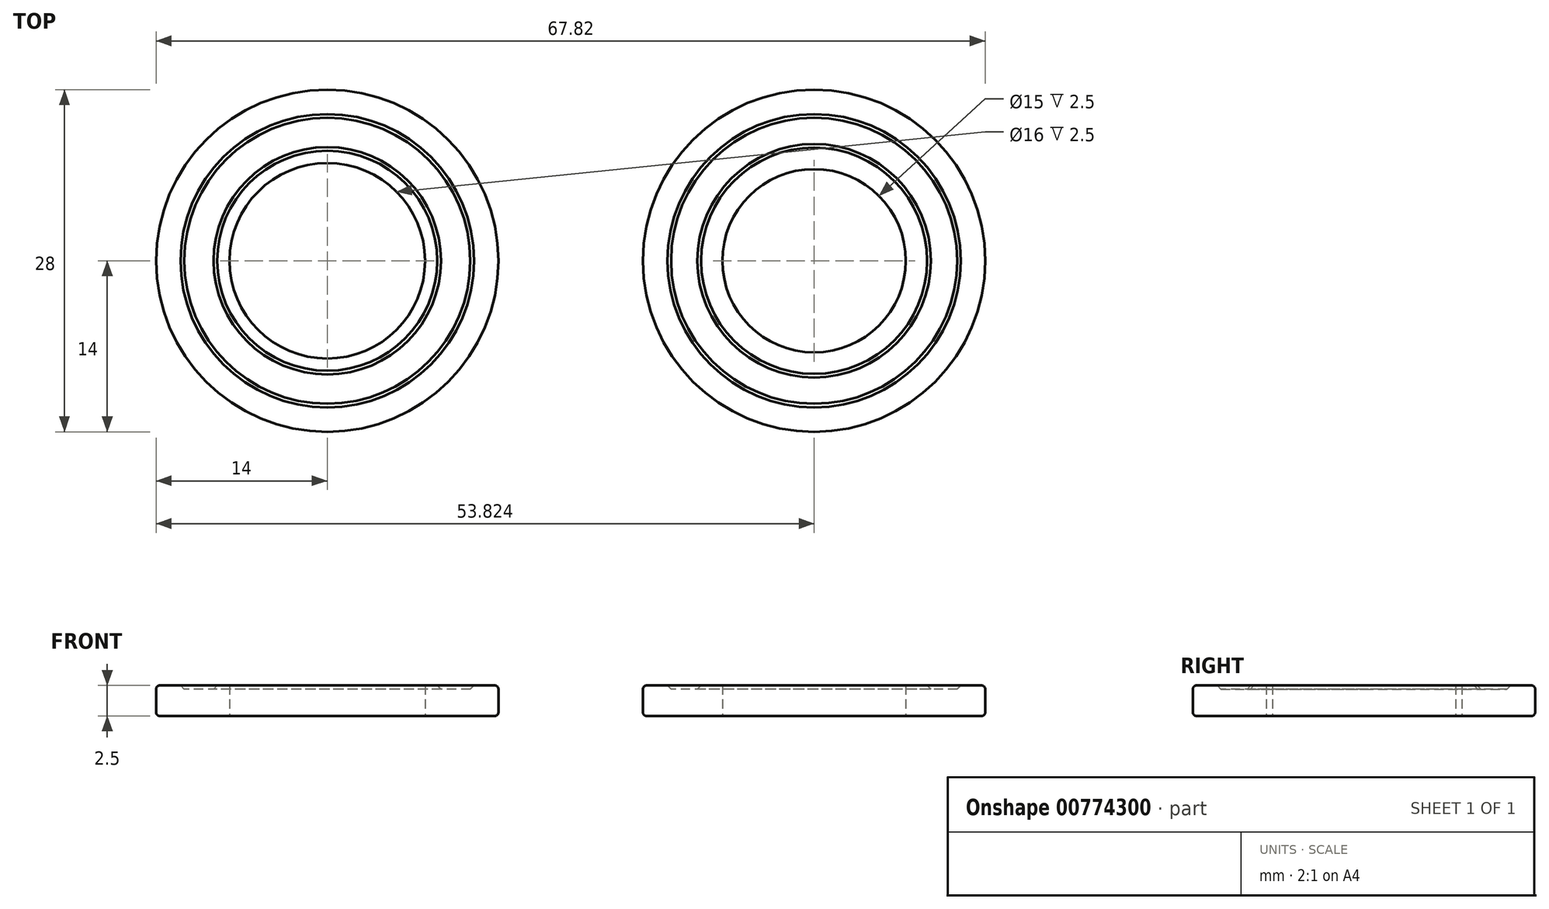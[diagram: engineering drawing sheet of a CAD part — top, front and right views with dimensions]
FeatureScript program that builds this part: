
annotation { "Feature Type Name" : "Feature", "Feature Type Description" : "" }
export const myFeature = defineFeature(function(context is Context, id is Id, definition is map)
    precondition{}
    {
        {
            var Q0;
            Q0=qCreatedBy(makeId("Top.planeOp"),FACE);
            var sketch = newSketch(context, id + "F0", { "sketchPlane" : qUnion([Q0])});
            skCircle(sketch, "E0", {"center": v(0, 0) * mm, "radius": 14 * mm});
            skCircle(sketch, "E1", {"center": v(0, 0) * mm, "radius": 8 * mm});
            skSolve(sketch);
        }
        {
            var Q0;
            Q0 = qSketchRegion(id + "F0", true);
            extrude(context, id + "F1", {"entities" : qUnion([Q0]), "depth" : 2.5 * mm, "offsetDistance" : 25 * mm});
        }
        {
            var Q0;
            Q0=makeQuery(id+"F1.opExtrude","CAP_FACE",FACE,{"disambiguationData":[OSD([sQuery(id+"F0.wireOp",EDGE,"E0"),sQuery(id+"F0.wireOp",EDGE,"E1")])],"isStart":false});
            var sketch = newSketch(context, id + "F2", { "sketchPlane" : qUnion([Q0])});
            skCircle(sketch, "E2", {"center": v(0, 0) * mm, "radius": 12 * mm});
            skCircle(sketch, "E3", {"center": v(0, 0) * mm, "radius": 9 * mm});
            skSolve(sketch);
        }
        {
            var Q0;
            Q0=makeQuery(id+"F2.imprint","IMPRINT",FACE,{"disambiguationData":[TD([[makeQuery(id+"F2.imprint","IMPRINT",EDGE,{"derivedFrom":sQuery(id+"F2.wireOp",EDGE,"E2")}),1.0]])]});
            extrude(context, id + "F3", {"entities" : qUnion([Q0]), "operationType" : NewBodyOperationType.REMOVE, "oppositeDirection" : true, "depth" : .3 * mm, "offsetDistance" : 25 * mm, "hasDraft" : true, "draftAngle" : 45 * degree, "draftPullDirection" : true});
        }
        {
            var Q0;
            Q0=makeQuery(id+"F1.opExtrude","CAP_EDGE",EDGE,{"disambiguationData":[OSD([sQuery(id+"F0.wireOp",EDGE,"E0")])],"isStart":false});
            var Q1;
            Q1=makeQuery(id+"F1.opExtrude","CAP_EDGE",EDGE,{"disambiguationData":[OSD([sQuery(id+"F0.wireOp",EDGE,"E0")])],"isStart":true});
            fillet(context, id + "F4", {"entities" : qUnion([Q0, Q1]), "radius" : .3 * mm, "tangentPropagation" : true, "allowEdgeOverflow" : false});
        }
        {
            var Q0;
            Q0=qCreatedBy(makeId("Top.planeOp"),FACE);
            var sketch = newSketch(context, id + "F5", { "sketchPlane" : qUnion([Q0])});
            skCircle(sketch, "E4", {"center": v(39.82, 0) * mm, "radius": 14 * mm});
            skCircle(sketch, "E5", {"center": v(39.82, 0) * mm, "radius": 7.5 * mm});
            skSolve(sketch);
        }
        {
            var Q0;
            Q0 = qSketchRegion(id + "F5", true);
            extrude(context, id + "F6", {"entities" : qUnion([Q0]), "depth" : 2.5 * mm, "offsetDistance" : 25 * mm});
        }
        {
            var Q0;
            Q0=makeQuery(id+"F6.opExtrude","CAP_FACE",FACE,{"disambiguationData":[OSD([sQuery(id+"F5.wireOp",EDGE,"E4"),sQuery(id+"F5.wireOp",EDGE,"E5")])],"isStart":false});
            var sketch = newSketch(context, id + "F7", { "sketchPlane" : qUnion([Q0])});
            skCircle(sketch, "E6", {"center": v(39.82, 0) * mm, "radius": 9.25 * mm});
            skCircle(sketch, "E7", {"center": v(39.82, 0) * mm, "radius": 12 * mm});
            skSolve(sketch);
        }
        {
            var Q0;
            Q0=makeQuery(id+"F7.imprint","IMPRINT",FACE,{"disambiguationData":[TD([[makeQuery(id+"F7.imprint","IMPRINT",EDGE,{"derivedFrom":sQuery(id+"F7.wireOp",EDGE,"E6")}),-1.0]])]});
            extrude(context, id + "F8", {"entities" : qUnion([Q0]), "operationType" : NewBodyOperationType.REMOVE, "oppositeDirection" : true, "depth" : .3 * mm, "offsetDistance" : 25 * mm, "hasDraft" : true, "draftAngle" : 45 * degree, "draftPullDirection" : true});
        }
        {
            var Q0;
            Q0=makeQuery(id+"F6.opExtrude","CAP_EDGE",EDGE,{"disambiguationData":[OSD([sQuery(id+"F5.wireOp",EDGE,"E4")])],"isStart":false});
            var Q1;
            Q1=makeQuery(id+"F6.opExtrude","CAP_EDGE",EDGE,{"disambiguationData":[OSD([sQuery(id+"F5.wireOp",EDGE,"E4")])],"isStart":true});
            fillet(context, id + "F9", {"entities" : qUnion([Q0, Q1]), "radius" : .3 * mm, "tangentPropagation" : true, "allowEdgeOverflow" : false});
        }
        {
            var Q0;
            Q0=makeQuery(id+"F3.boolean.opBoolean","COPY",FACE,{"derivedFrom":makeQuery(id+"F3.opExtrude","CAP_FACE",FACE,{"disambiguationData":[OSD([sQuery(id+"F2.wireOp",EDGE,"E2"),sQuery(id+"F2.wireOp",EDGE,"E3")])],"isStart":false})});
            var sketch = newSketch(context, id + "F10", { "sketchPlane" : qUnion([Q0])});
            skLineSegment(sketch, "E8", {"start": v(0, 11.7) * mm, "end": v(0, 9.3) * mm});
            skPoint(sketch, "E9", {"position": v(0, 10.5) * mm});
            skSolve(sketch);
        }
    });
